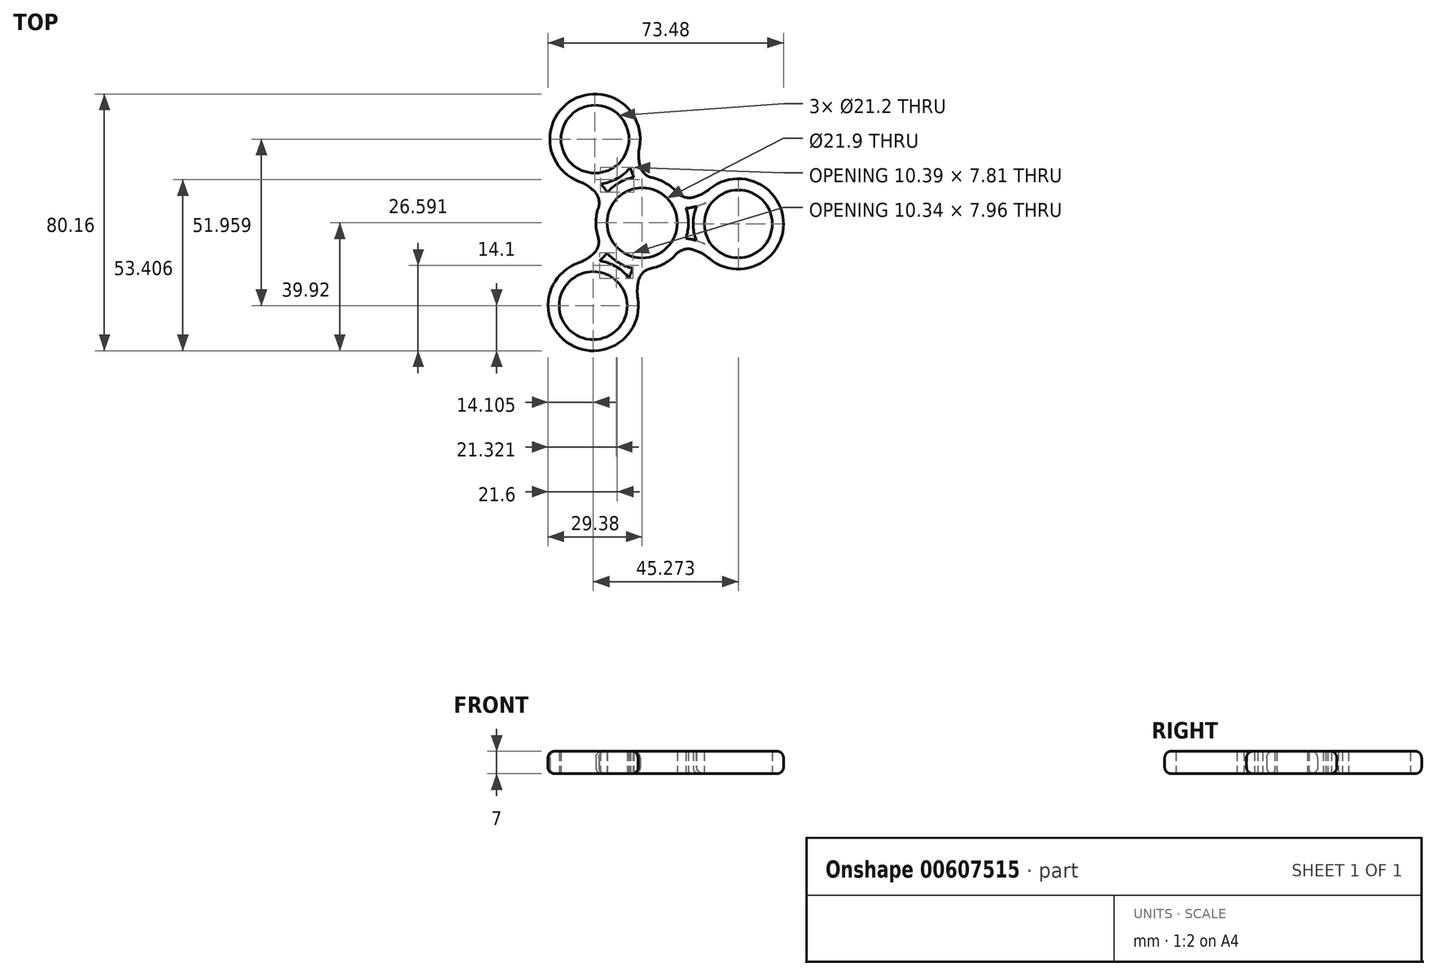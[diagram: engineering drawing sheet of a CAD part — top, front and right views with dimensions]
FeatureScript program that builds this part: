
annotation { "Feature Type Name" : "Feature", "Feature Type Description" : "" }
export const myFeature = defineFeature(function(context is Context, id is Id, definition is map)
    precondition{}
    {
        {
            var Q0;
            Q0=qCreatedBy(makeId("Top.planeOp"),FACE);
            var sketch = newSketch(context, id + "F0", { "sketchPlane" : qUnion([Q0])});
            skCircle(sketch, "E0", {"center": v(0, 0) * mm, "radius": 10.95 * mm});
            skCircle(sketch, "E1.0", {"center": v(0, 0) * mm, "radius": 14.45 * mm});
            skCircle(sketch, "E2.cCircle", {"center": v(0, 0) * mm, "radius": 15 * mm, "construction": true});
            skLineSegment(sketch, "E2.0", {"start": v(-14.72, 26.14) * mm, "end": v(30, -0.32) * mm, "construction": true});
            skLineSegment(sketch, "E2.1", {"start": v(30, -0.32) * mm, "end": v(-15.28, -25.82) * mm, "construction": true});
            skLineSegment(sketch, "E2.2", {"start": v(-15.28, -25.82) * mm, "end": v(-14.72, 26.14) * mm, "construction": true});
            skPoint(sketch, "E2.0.midPoint", {"position": v(7.64, 12.9) * mm});
            skCircle(sketch, "E3", {"center": v(-14.72, 26.14) * mm, "radius": 10.6 * mm});
            skCircle(sketch, "E4", {"center": v(30, -0.32) * mm, "radius": 10.6 * mm});
            skCircle(sketch, "E5", {"center": v(-15.28, -25.82) * mm, "radius": 10.6 * mm});
            skCircle(sketch, "E6.0", {"center": v(-14.72, 26.14) * mm, "radius": 14.1 * mm});
            skCircle(sketch, "E7.0", {"center": v(-15.28, -25.82) * mm, "radius": 14.1 * mm});
            skCircle(sketch, "E8.0", {"center": v(30, -0.32) * mm, "radius": 14.1 * mm});
            skArc(sketch, "E9", {"start": v(-0.86, 23.57) * mm, "mid": v(5.58, 9.42) * mm, "end": v(21.07, 10.6) * mm});
            skArc(sketch, "E10", {"start": v(20.84, -11.04) * mm, "mid": v(5.37, -9.54) * mm, "end": v(-1.36, -23.55) * mm});
            skArc(sketch, "E11", {"start": v(-19.99, -12.53) * mm, "mid": v(-10.95, 0.12) * mm, "end": v(-19.71, 12.95) * mm});
            skArc(sketch, "E12.0", {"start": v(-18.98, -15.36) * mm, "mid": v(-7.95, 0.08) * mm, "end": v(-18.65, 15.76) * mm});
            skArc(sketch, "E13.0", {"start": v(-3.8, 24.12) * mm, "mid": v(4.05, 6.84) * mm, "end": v(22.97, 8.27) * mm});
            skArc(sketch, "E14.0", {"start": v(22.8, -8.76) * mm, "mid": v(3.9, -6.93) * mm, "end": v(-4.32, -24.03) * mm});
            skSolve(sketch);
        }
        {
            var Q0;
            Q0 = qSketchRegion(id + "F0", true);
            var Q1;
            {var subQ0=sQuery(id+"F0.wireOp",EDGE,"E13.0");var subQ1=sQuery(id+"F0.wireOp",EDGE,"E0");var subQ2=makeQuery(id+"F0.imprint","INTERSECT",VERTEX,{"disambiguationData":[OD(1.0)],"derivedFrom":[subQ1,subQ0]});Q1=makeQuery(id+"F0.imprint","IMPRINT",FACE,{"disambiguationData":[TD([[makeQuery(id+"F0.imprint","IMPRINT",EDGE,{"disambiguationData":[TD([[subQ2,-1.0]])],"derivedFrom":subQ1}),-1.0]])]});}
            var Q2;
            {var subQ0=sQuery(id+"F0.wireOp",EDGE,"E13.0");var subQ1=sQuery(id+"F0.wireOp",EDGE,"E0");var subQ2=makeQuery(id+"F0.imprint","INTERSECT",VERTEX,{"disambiguationData":[OD(0.0)],"derivedFrom":[subQ1,subQ0]});Q2=makeQuery(id+"F0.imprint","IMPRINT",FACE,{"disambiguationData":[TD([[makeQuery(id+"F0.imprint","IMPRINT",EDGE,{"disambiguationData":[TD([[subQ2,1.0]])],"derivedFrom":subQ1}),-1.0]])]});}
            var Q3;
            {var subQ0=sQuery(id+"F0.wireOp",EDGE,"E12.0");var subQ1=sQuery(id+"F0.wireOp",EDGE,"E0");var subQ2=makeQuery(id+"F0.imprint","INTERSECT",VERTEX,{"disambiguationData":[OD(1.0)],"derivedFrom":[subQ1,subQ0]});Q3=makeQuery(id+"F0.imprint","IMPRINT",FACE,{"disambiguationData":[TD([[makeQuery(id+"F0.imprint","IMPRINT",EDGE,{"disambiguationData":[TD([[subQ2,-1.0]])],"derivedFrom":subQ1}),-1.0]])]});}
            extrude(context, id + "F1", {"entities" : qUnion([Q0, Q1, Q2, Q3]), "depth" : 7 * mm, "offsetDistance" : 25 * mm});
        }
        {
            var Q0;
            {var subQ0=sQuery(id+"F0.wireOp",EDGE,"E10");var subQ1=sQuery(id+"F0.wireOp",EDGE,"E1.0");Q0=makeQuery(id+"F1.opExtrude","SWEPT_EDGE",EDGE,{"disambiguationData":[OSD([subQ1,subQ0]),TDD([makeQuery(id+"F0.imprint","INTERSECT",VERTEX,{"disambiguationData":[OD(0.0)],"derivedFrom":[subQ1,subQ0]})])]});}
            var Q1;
            {var subQ0=sQuery(id+"F0.wireOp",EDGE,"E10");var subQ1=sQuery(id+"F0.wireOp",EDGE,"E1.0");Q1=makeQuery(id+"F1.opExtrude","SWEPT_EDGE",EDGE,{"disambiguationData":[OSD([subQ1,subQ0]),TDD([makeQuery(id+"F0.imprint","INTERSECT",VERTEX,{"disambiguationData":[OD(1.0)],"derivedFrom":[subQ1,subQ0]})])]});}
            var Q2;
            {var subQ0=sQuery(id+"F0.wireOp",EDGE,"E9");var subQ1=sQuery(id+"F0.wireOp",EDGE,"E1.0");Q2=makeQuery(id+"F1.opExtrude","SWEPT_EDGE",EDGE,{"disambiguationData":[OSD([subQ1,subQ0]),TDD([makeQuery(id+"F0.imprint","INTERSECT",VERTEX,{"disambiguationData":[OD(1.0)],"derivedFrom":[subQ1,subQ0]})])]});}
            var Q3;
            {var subQ0=sQuery(id+"F0.wireOp",EDGE,"E9");var subQ1=sQuery(id+"F0.wireOp",EDGE,"E1.0");Q3=makeQuery(id+"F1.opExtrude","SWEPT_EDGE",EDGE,{"disambiguationData":[OSD([subQ1,subQ0]),TDD([makeQuery(id+"F0.imprint","INTERSECT",VERTEX,{"disambiguationData":[OD(0.0)],"derivedFrom":[subQ1,subQ0]})])]});}
            var Q4;
            {var subQ0=sQuery(id+"F0.wireOp",EDGE,"E11");var subQ1=sQuery(id+"F0.wireOp",EDGE,"E1.0");Q4=makeQuery(id+"F1.opExtrude","SWEPT_EDGE",EDGE,{"disambiguationData":[OSD([subQ1,subQ0]),TDD([makeQuery(id+"F0.imprint","INTERSECT",VERTEX,{"disambiguationData":[OD(1.0)],"derivedFrom":[subQ1,subQ0]})])]});}
            var Q5;
            {var subQ0=sQuery(id+"F0.wireOp",EDGE,"E11");var subQ1=sQuery(id+"F0.wireOp",EDGE,"E1.0");Q5=makeQuery(id+"F1.opExtrude","SWEPT_EDGE",EDGE,{"disambiguationData":[OSD([subQ1,subQ0]),TDD([makeQuery(id+"F0.imprint","INTERSECT",VERTEX,{"disambiguationData":[OD(0.0)],"derivedFrom":[subQ1,subQ0]})])]});}
            fillet(context, id + "F2", {"entities" : qUnion([Q0, Q1, Q2, Q3, Q4, Q5]), "radius" : 5 * mm, "tangentPropagation" : true, "allowEdgeOverflow" : false});
        }
        {
            var Q0;
            Q0=makeQuery(id+"F1.opExtrude","CAP_EDGE",EDGE,{"disambiguationData":[OSD([sQuery(id+"F0.wireOp",EDGE,"E8.0")])],"isStart":true});
            var Q1;
            {var subQ0=sQuery(id+"F0.wireOp",EDGE,"E10");var subQ1=sQuery(id+"F0.wireOp",EDGE,"E1.0");Q1=makeQuery(id+"F1.opExtrude","CAP_EDGE",EDGE,{"disambiguationData":[OSD([subQ1]),TDD([makeQuery(id+"F0.imprint","IMPRINT",EDGE,{"disambiguationData":[TD([[makeQuery(id+"F0.imprint","INTERSECT",VERTEX,{"disambiguationData":[OD(0.0)],"derivedFrom":[subQ1,subQ0]}),-1.0]])],"derivedFrom":subQ1})])],"isStart":false});}
            fillet(context, id + "F3", {"entities" : qUnion([Q0, Q1]), "radius" : 2 * mm, "tangentPropagation" : true, "allowEdgeOverflow" : false});
        }
    });
